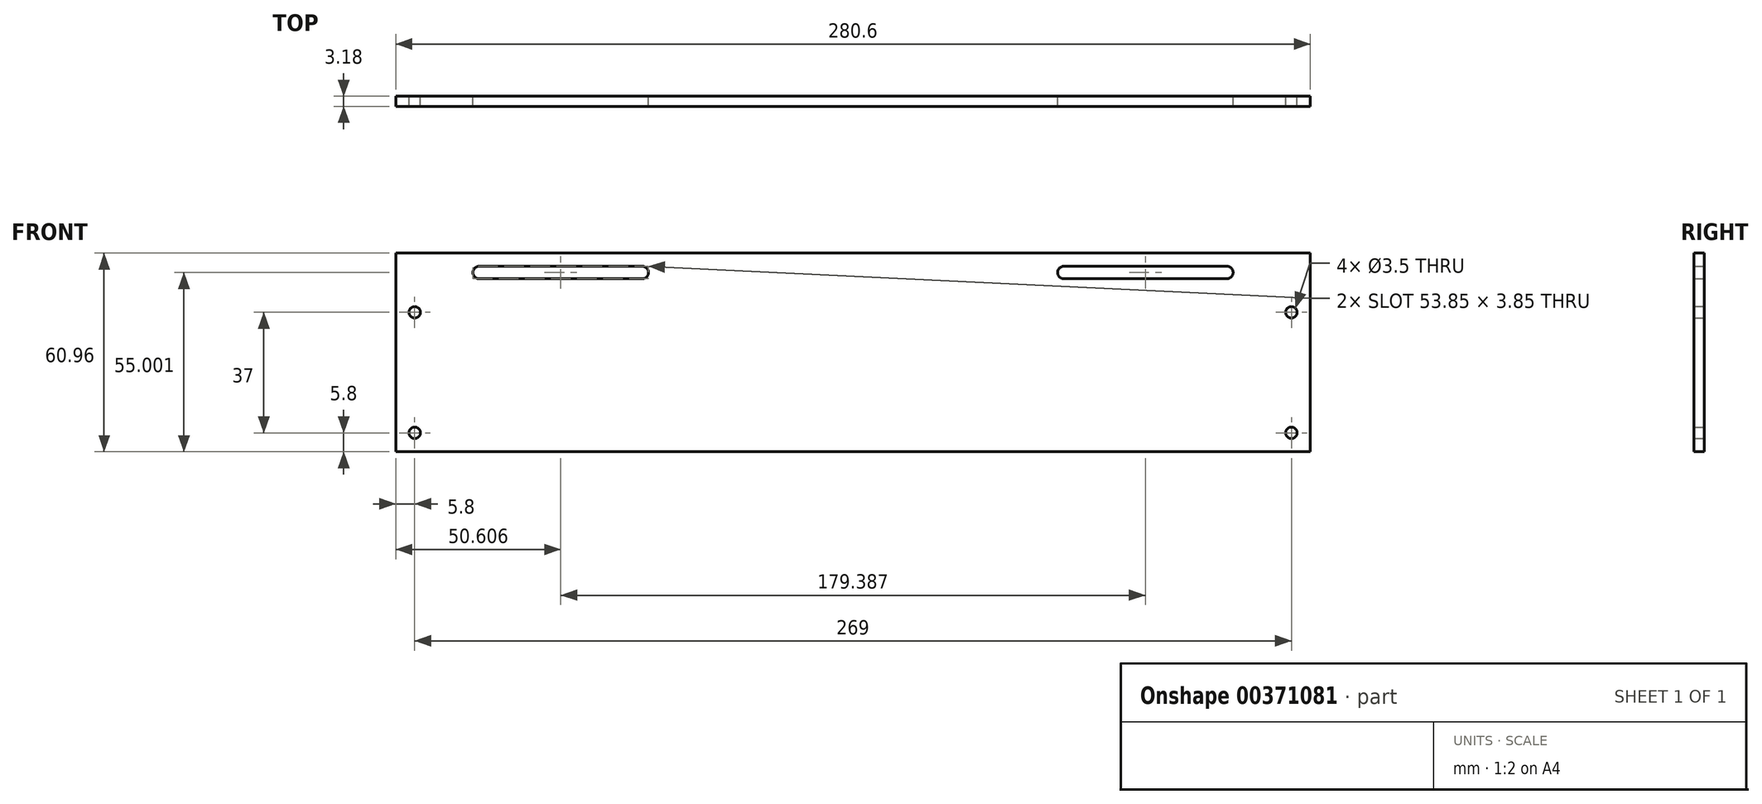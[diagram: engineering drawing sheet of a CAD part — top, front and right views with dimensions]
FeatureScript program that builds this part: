
annotation { "Feature Type Name" : "Feature", "Feature Type Description" : "" }
export const myFeature = defineFeature(function(context is Context, id is Id, definition is map)
    precondition{}
    {
        {
            var Q0;
            Q0=qCreatedBy(makeId("Front.planeOp"),FACE);
            var sketch = newSketch(context, id + "F0", { "sketchPlane" : qUnion([Q0])});
            skLineSegment(sketch, "E0.bottom", {"start": v(140.3, 30.48) * mm, "end": v(-140.3, 30.48) * mm});
            skLineSegment(sketch, "E0.top", {"start": v(140.3, -30.48) * mm, "end": v(-140.3, -30.48) * mm});
            skLineSegment(sketch, "E0.left", {"start": v(140.3, 30.48) * mm, "end": v(140.3, -30.48) * mm});
            skLineSegment(sketch, "E0.right", {"start": v(-140.3, 30.48) * mm, "end": v(-140.3, -30.48) * mm});
            skPoint(sketch, "E0.middle", {"position": v(0, 0) * mm});
            skCircle(sketch, "E1", {"center": v(-89.7, 24.52) * mm, "radius": 1.93 * mm});
            skLineSegment(sketch, "E2", {"start": v(-114.7, 24.52) * mm, "end": v(-64.7, 24.52) * mm});
            skArc(sketch, "E3.0.startCap", {"start": v(-114.7, 22.6) * mm, "mid": v(-116.62, 24.52) * mm, "end": v(-114.7, 26.45) * mm});
            skArc(sketch, "E3.0.endCap", {"start": v(-64.7, 26.45) * mm, "mid": v(-62.77, 24.52) * mm, "end": v(-64.7, 22.6) * mm});
            skLineSegment(sketch, "E3.0.left", {"start": v(-114.7, 26.45) * mm, "end": v(-64.7, 26.45) * mm});
            skLineSegment(sketch, "E3.0.right", {"start": v(-114.7, 22.6) * mm, "end": v(-64.7, 22.6) * mm});
            skArc(sketch, "E4.MirrorCS", {"start": v(64.7, 26.45) * mm, "mid": v(62.77, 24.52) * mm, "end": v(64.7, 22.6) * mm});
            skLineSegment(sketch, "E5.MirrorCS", {"start": v(114.7, 22.6) * mm, "end": v(64.7, 22.6) * mm});
            skArc(sketch, "E6.MirrorCS", {"start": v(114.7, 22.6) * mm, "mid": v(116.62, 24.52) * mm, "end": v(114.7, 26.45) * mm});
            skLineSegment(sketch, "E7.MirrorCS", {"start": v(114.7, 26.45) * mm, "end": v(64.7, 26.45) * mm});
            skPoint(sketch, "E8", {"position": v(89.7, 24.52) * mm});
            skPoint(sketch, "E8.positionSnap0", {"position": v(89.7, 26.45) * mm});
            skCircle(sketch, "E9", {"center": v(-134.5, -24.68) * mm, "radius": 1.75 * mm});
            skCircle(sketch, "E10", {"center": v(-134.5, 12.32) * mm, "radius": 1.75 * mm});
            skCircle(sketch, "E11.MirrorC", {"center": v(134.5, -24.68) * mm, "radius": 1.75 * mm});
            skCircle(sketch, "E12.MirrorC", {"center": v(134.5, 12.32) * mm, "radius": 1.75 * mm});
            skLineSegment(sketch, "E13", {"start": v(-134.5, -24.68) * mm, "end": v(-134.5, -30.48) * mm});
            skLineSegment(sketch, "E14", {"start": v(-134.5, -24.68) * mm, "end": v(-140.3, -24.68) * mm});
            skSolve(sketch);
        }
        {
            var Q0;
            Q0=qSketchRegion(id+"F0",true);
            extrude(context, id + "F1", {"entities" : qUnion([Q0]), "endBound" : BoundingType.SYMMETRIC, "depth" : 3.17 * mm});
        }
    });
